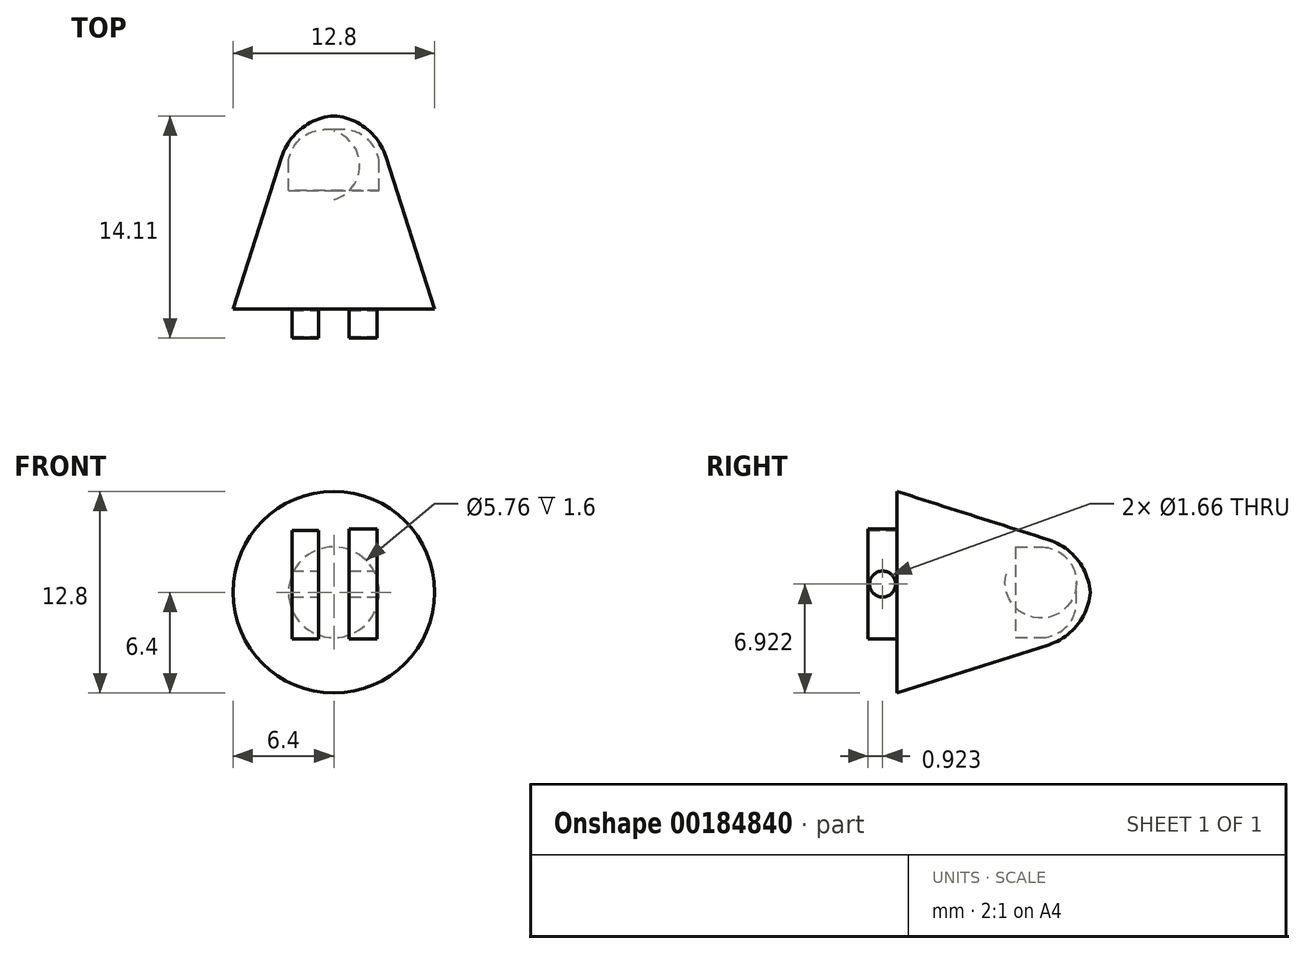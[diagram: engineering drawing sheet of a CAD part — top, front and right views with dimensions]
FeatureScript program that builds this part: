
annotation { "Feature Type Name" : "Feature", "Feature Type Description" : "" }
export const myFeature = defineFeature(function(context is Context, id is Id, definition is map)
    precondition{}
    {
        {
            var Q0;
            Q0=qCreatedBy(makeId("Top.planeOp"),FACE);
            var sketch = newSketch(context, id + "F0", { "sketchPlane" : qUnion([Q0])});
            skLineSegment(sketch, "E0", {"start": v(-6.4, 0) * mm, "end": v(-3.33, 9.63) * mm});
            skLineSegment(sketch, "E1", {"start": v(0, 0) * mm, "end": v(0, 12.26) * mm, "construction": true});
            skArc(sketch, "E2", {"start": v(-3.33, 9.63) * mm, "mid": v(-2.07, 11.46) * mm, "end": v(0, 12.26) * mm});
            skLineSegment(sketch, "E3", {"start": v(-2.88, 7.52) * mm, "end": v(-2.88, 9.12) * mm});
            skLineSegment(sketch, "E4", {"start": v(-2.88, 7.52) * mm, "end": v(0, 7.52) * mm});
            skArc(sketch, "E5", {"start": v(-2.88, 9.12) * mm, "mid": v(-1.98, 10.93) * mm, "end": v(0, 11.3) * mm});
            skLineSegment(sketch, "E6", {"start": v(-6.4, 0) * mm, "end": v(0, 0) * mm});
            skLineSegment(sketch, "E7", {"start": v(0, 12.26) * mm, "end": v(0, 0.87) * mm});
            skLineSegment(sketch, "E8", {"start": v(0, 0.87) * mm, "end": v(0, 0) * mm});
            skSolve(sketch);
        }
        {
            var Q0;
            Q0=makeQuery(id+"F0.imprint","IMPRINT",FACE,{"disambiguationData":[TD([[makeQuery(id+"F0.imprint","IMPRINT",EDGE,{"derivedFrom":sQuery(id+"F0.wireOp",EDGE,"E0")}),-1.0]])]});
            var Q1;
            Q1=sQuery(id+"F0.wireOp",EDGE,"E7");
            revolve(context, id + "F1", {"entities" : qUnion([Q0]), "axis" : qUnion([Q1]), "revolveType" : RevolveType.FULL});
        }
        {
            var Q0;
            Q0=makeQuery(id+"F1.opRevolve","SWEPT_FACE",FACE,{"disambiguationData":[OSD([sQuery(id+"F0.wireOp",EDGE,"E6")])]});
            var sketch = newSketch(context, id + "F2", { "sketchPlane" : qUnion([Q0])});
            skLineSegment(sketch, "E9.bottom", {"start": v(-0.95, 3.94) * mm, "end": v(-2.66, 3.94) * mm});
            skLineSegment(sketch, "E9.top", {"start": v(-0.95, -2.96) * mm, "end": v(-2.66, -2.96) * mm});
            skLineSegment(sketch, "E9.left", {"start": v(-0.95, 3.94) * mm, "end": v(-0.95, -2.96) * mm});
            skLineSegment(sketch, "E9.right", {"start": v(-2.66, 3.94) * mm, "end": v(-2.66, -2.96) * mm});
            skLineSegment(sketch, "E10.bottom", {"start": v(0.97, 4) * mm, "end": v(2.75, 4) * mm});
            skLineSegment(sketch, "E10.top", {"start": v(0.97, -2.96) * mm, "end": v(2.75, -2.96) * mm});
            skLineSegment(sketch, "E10.left", {"start": v(0.97, 4) * mm, "end": v(0.97, -2.96) * mm});
            skLineSegment(sketch, "E10.right", {"start": v(2.75, 4) * mm, "end": v(2.75, -2.96) * mm});
            skSolve(sketch);
        }
        {
            var Q0;
            Q0=makeQuery(id+"F2.imprint","IMPRINT",FACE,{"disambiguationData":[TD([[makeQuery(id+"F2.imprint","IMPRINT",EDGE,{"derivedFrom":sQuery(id+"F2.wireOp",EDGE,"E9.bottom")}),1.0]])]});
            var Q1;
            Q1=makeQuery(id+"F2.imprint","IMPRINT",FACE,{"disambiguationData":[TD([[makeQuery(id+"F2.imprint","IMPRINT",EDGE,{"derivedFrom":sQuery(id+"F2.wireOp",EDGE,"E10.bottom")}),-1.0]])]});
            extrude(context, id + "F3", {"entities" : qUnion([Q0, Q1]), "operationType" : NewBodyOperationType.ADD, "depth" : 1.85 * mm});
        }
        {
            var Q0;
            Q0=makeQuery(id+"F3.opExtrude","SWEPT_FACE",FACE,{"disambiguationData":[OSD([sQuery(id+"F2.wireOp",EDGE,"E10.right")])]});
            var sketch = newSketch(context, id + "F4", { "sketchPlane" : qUnion([Q0])});
            skLineSegment(sketch, "E11", {"start": v(-0.93, 4) * mm, "end": v(-0.93, -2.96) * mm, "construction": true});
            skCircle(sketch, "E12", {"center": v(-0.93, 0.52) * mm, "radius": 0.83 * mm});
            skSolve(sketch);
        }
        {
            var Q0;
            Q0=makeQuery(id+"F4.imprint","IMPRINT",FACE,{"disambiguationData":[TD([[makeQuery(id+"F4.imprint","IMPRINT",EDGE,{"derivedFrom":sQuery(id+"F4.wireOp",EDGE,"E12")}),1.0]])]});
            var Q1;
            Q1=sQuery(id+"F4.wireOp",EDGE,"E12");
            extrude(context, id + "F5", {"entities" : qUnion([Q0]), "operationType" : NewBodyOperationType.REMOVE, "surfaceEntities" : qUnion([Q1]), "oppositeDirection" : true, "depth" : 10 * mm});
        }
    });
